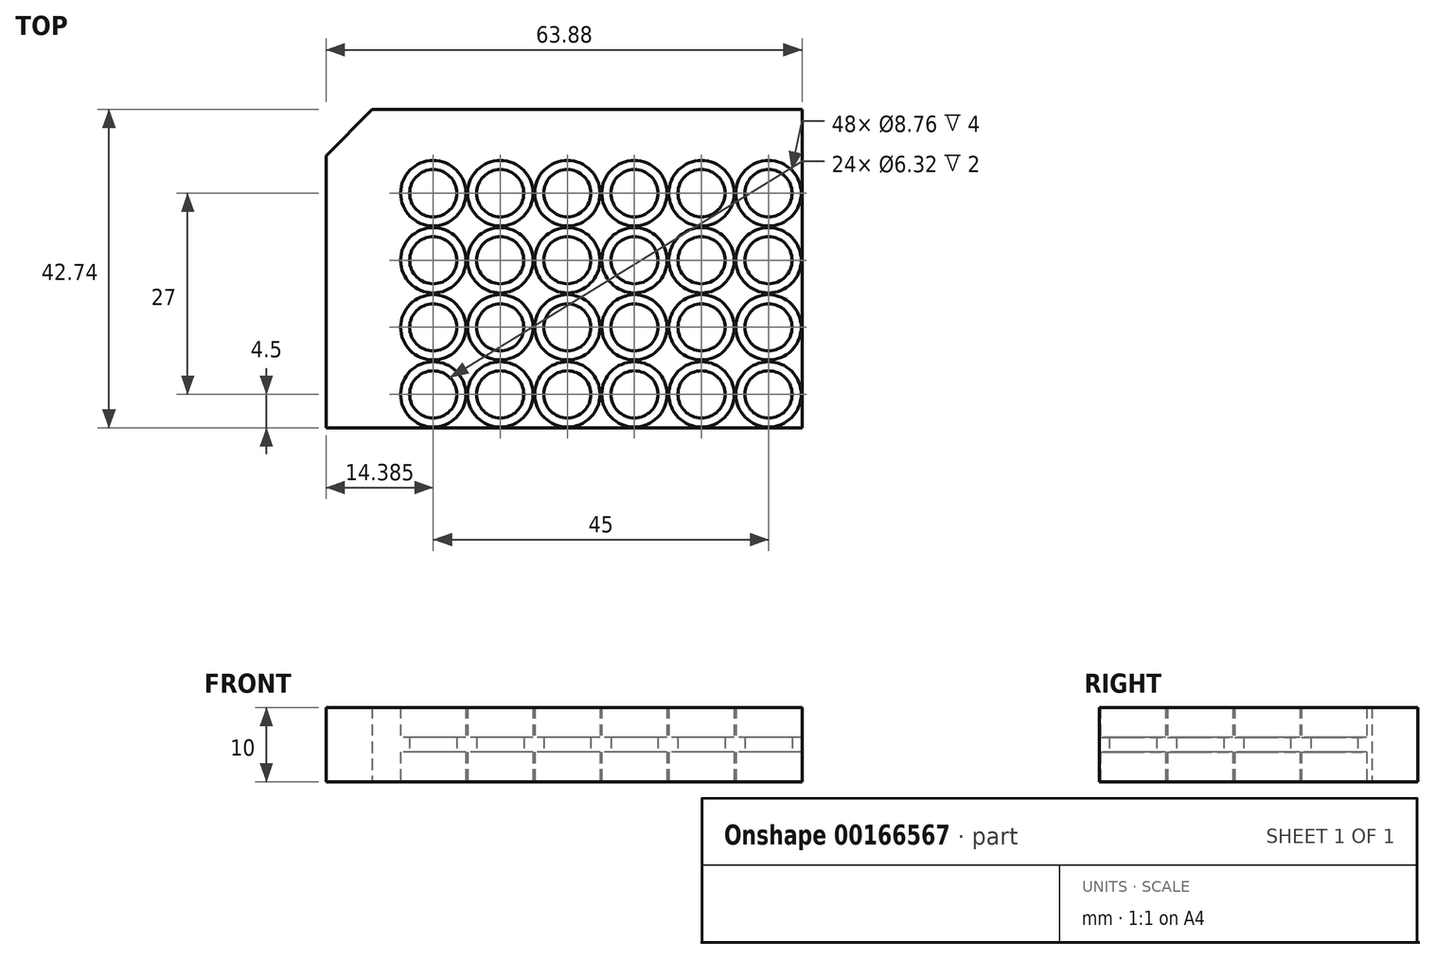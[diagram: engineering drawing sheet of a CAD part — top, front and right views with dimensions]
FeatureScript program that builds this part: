
annotation { "Feature Type Name" : "Feature", "Feature Type Description" : "" }
export const myFeature = defineFeature(function(context is Context, id is Id, definition is map)
    precondition{}
    {
        {
            var Q0;
            Q0=qCreatedBy(makeId("Top.planeOp"),FACE);
            var sketch = newSketch(context, id + "F0", { "sketchPlane" : qUnion([Q0])});
            skLineSegment(sketch, "E0", {"start": v(-63.88, 36.54) * mm, "end": v(-63.88, -36.54) * mm});
            skLineSegment(sketch, "E1", {"start": v(-63.88, -36.54) * mm, "end": v(-57.68, -42.74) * mm});
            skLineSegment(sketch, "E2", {"start": v(-57.68, -42.74) * mm, "end": v(63.88, -42.74) * mm});
            skLineSegment(sketch, "E3", {"start": v(63.88, -42.74) * mm, "end": v(63.88, 42.74) * mm});
            skLineSegment(sketch, "E4", {"start": v(63.88, 42.74) * mm, "end": v(-57.68, 42.74) * mm});
            skLineSegment(sketch, "E5", {"start": v(-57.68, 42.74) * mm, "end": v(-63.88, 36.54) * mm});
            skPoint(sketch, "E6", {"position": v(-63.87, 0) * mm});
            skLineSegment(sketch, "E7", {"start": v(-63.87, 0) * mm, "end": v(63.87, 0) * mm, "construction": true});
            skLineSegment(sketch, "E8", {"start": v(0, -42.74) * mm, "end": v(0, 42.74) * mm, "construction": true});
            skPoint(sketch, "E9", {"position": v(0, 0) * mm});
            skLineSegment(sketch, "E10", {"start": v(-63.88, 36.54) * mm, "end": v(-63.88, 42.74) * mm, "construction": true});
            skLineSegment(sketch, "E11", {"start": v(-63.88, 42.74) * mm, "end": v(-57.68, 42.74) * mm, "construction": true});
            skCircle(sketch, "E12", {"center": v(-49.5, 31.5) * mm, "radius": 3.16 * mm});
            skCircle(sketch, "E13.0.1.0", {"center": v(-49.5, 22.5) * mm, "radius": 3.16 * mm});
            skCircle(sketch, "E13.0.2.0", {"center": v(-49.5, 13.5) * mm, "radius": 3.16 * mm});
            skCircle(sketch, "E13.0.3.0", {"center": v(-49.5, 4.5) * mm, "radius": 3.16 * mm});
            skCircle(sketch, "E13.0.4.0", {"center": v(-49.5, -4.5) * mm, "radius": 3.16 * mm});
            skCircle(sketch, "E13.0.5.0", {"center": v(-49.5, -13.5) * mm, "radius": 3.16 * mm});
            skCircle(sketch, "E13.0.6.0", {"center": v(-49.5, -22.5) * mm, "radius": 3.16 * mm});
            skCircle(sketch, "E13.0.7.0", {"center": v(-49.5, -31.5) * mm, "radius": 3.16 * mm});
            skCircle(sketch, "E13.1.0.0", {"center": v(-40.5, 31.5) * mm, "radius": 3.16 * mm});
            skCircle(sketch, "E13.1.1.0", {"center": v(-40.5, 22.5) * mm, "radius": 3.16 * mm});
            skCircle(sketch, "E13.1.2.0", {"center": v(-40.5, 13.5) * mm, "radius": 3.16 * mm});
            skCircle(sketch, "E13.1.3.0", {"center": v(-40.5, 4.5) * mm, "radius": 3.16 * mm});
            skCircle(sketch, "E13.1.4.0", {"center": v(-40.5, -4.5) * mm, "radius": 3.16 * mm});
            skCircle(sketch, "E13.1.5.0", {"center": v(-40.5, -13.5) * mm, "radius": 3.16 * mm});
            skCircle(sketch, "E13.1.6.0", {"center": v(-40.5, -22.5) * mm, "radius": 3.16 * mm});
            skCircle(sketch, "E13.1.7.0", {"center": v(-40.5, -31.5) * mm, "radius": 3.16 * mm});
            skCircle(sketch, "E13.2.0.0", {"center": v(-31.5, 31.5) * mm, "radius": 3.16 * mm});
            skCircle(sketch, "E13.2.1.0", {"center": v(-31.5, 22.5) * mm, "radius": 3.16 * mm});
            skCircle(sketch, "E13.2.2.0", {"center": v(-31.5, 13.5) * mm, "radius": 3.16 * mm});
            skCircle(sketch, "E13.2.3.0", {"center": v(-31.5, 4.5) * mm, "radius": 3.16 * mm});
            skCircle(sketch, "E13.2.4.0", {"center": v(-31.5, -4.5) * mm, "radius": 3.16 * mm});
            skCircle(sketch, "E13.2.5.0", {"center": v(-31.5, -13.5) * mm, "radius": 3.16 * mm});
            skCircle(sketch, "E13.2.6.0", {"center": v(-31.5, -22.5) * mm, "radius": 3.16 * mm});
            skCircle(sketch, "E13.2.7.0", {"center": v(-31.5, -31.5) * mm, "radius": 3.16 * mm});
            skCircle(sketch, "E13.3.0.0", {"center": v(-22.5, 31.5) * mm, "radius": 3.16 * mm});
            skCircle(sketch, "E13.3.1.0", {"center": v(-22.5, 22.5) * mm, "radius": 3.16 * mm});
            skCircle(sketch, "E13.3.2.0", {"center": v(-22.5, 13.5) * mm, "radius": 3.16 * mm});
            skCircle(sketch, "E13.3.3.0", {"center": v(-22.5, 4.5) * mm, "radius": 3.16 * mm});
            skCircle(sketch, "E13.3.4.0", {"center": v(-22.5, -4.5) * mm, "radius": 3.16 * mm});
            skCircle(sketch, "E13.3.5.0", {"center": v(-22.5, -13.5) * mm, "radius": 3.16 * mm});
            skCircle(sketch, "E13.3.6.0", {"center": v(-22.5, -22.5) * mm, "radius": 3.16 * mm});
            skCircle(sketch, "E13.3.7.0", {"center": v(-22.5, -31.5) * mm, "radius": 3.16 * mm});
            skCircle(sketch, "E13.4.0.0", {"center": v(-13.5, 31.5) * mm, "radius": 3.16 * mm});
            skCircle(sketch, "E13.4.1.0", {"center": v(-13.5, 22.5) * mm, "radius": 3.16 * mm});
            skCircle(sketch, "E13.4.2.0", {"center": v(-13.5, 13.5) * mm, "radius": 3.16 * mm});
            skCircle(sketch, "E13.4.3.0", {"center": v(-13.5, 4.5) * mm, "radius": 3.16 * mm});
            skCircle(sketch, "E13.4.4.0", {"center": v(-13.5, -4.5) * mm, "radius": 3.16 * mm});
            skCircle(sketch, "E13.4.5.0", {"center": v(-13.5, -13.5) * mm, "radius": 3.16 * mm});
            skCircle(sketch, "E13.4.6.0", {"center": v(-13.5, -22.5) * mm, "radius": 3.16 * mm});
            skCircle(sketch, "E13.4.7.0", {"center": v(-13.5, -31.5) * mm, "radius": 3.16 * mm});
            skCircle(sketch, "E13.5.0.0", {"center": v(-4.5, 31.5) * mm, "radius": 3.16 * mm});
            skCircle(sketch, "E13.5.1.0", {"center": v(-4.5, 22.5) * mm, "radius": 3.16 * mm});
            skCircle(sketch, "E13.5.2.0", {"center": v(-4.5, 13.5) * mm, "radius": 3.16 * mm});
            skCircle(sketch, "E13.5.3.0", {"center": v(-4.5, 4.5) * mm, "radius": 3.16 * mm});
            skCircle(sketch, "E13.5.4.0", {"center": v(-4.5, -4.5) * mm, "radius": 3.16 * mm});
            skCircle(sketch, "E13.5.5.0", {"center": v(-4.5, -13.5) * mm, "radius": 3.16 * mm});
            skCircle(sketch, "E13.5.6.0", {"center": v(-4.5, -22.5) * mm, "radius": 3.16 * mm});
            skCircle(sketch, "E13.5.7.0", {"center": v(-4.5, -31.5) * mm, "radius": 3.16 * mm});
            skCircle(sketch, "E13.6.0.0", {"center": v(4.5, 31.5) * mm, "radius": 3.16 * mm});
            skCircle(sketch, "E13.6.1.0", {"center": v(4.5, 22.5) * mm, "radius": 3.16 * mm});
            skCircle(sketch, "E13.6.2.0", {"center": v(4.5, 13.5) * mm, "radius": 3.16 * mm});
            skCircle(sketch, "E13.6.3.0", {"center": v(4.5, 4.5) * mm, "radius": 3.16 * mm});
            skCircle(sketch, "E13.6.4.0", {"center": v(4.5, -4.5) * mm, "radius": 3.16 * mm});
            skCircle(sketch, "E13.6.5.0", {"center": v(4.5, -13.5) * mm, "radius": 3.16 * mm});
            skCircle(sketch, "E13.6.6.0", {"center": v(4.5, -22.5) * mm, "radius": 3.16 * mm});
            skCircle(sketch, "E13.6.7.0", {"center": v(4.5, -31.5) * mm, "radius": 3.16 * mm});
            skCircle(sketch, "E13.7.0.0", {"center": v(13.5, 31.5) * mm, "radius": 3.16 * mm});
            skCircle(sketch, "E13.7.1.0", {"center": v(13.5, 22.5) * mm, "radius": 3.16 * mm});
            skCircle(sketch, "E13.7.2.0", {"center": v(13.5, 13.5) * mm, "radius": 3.16 * mm});
            skCircle(sketch, "E13.7.3.0", {"center": v(13.5, 4.5) * mm, "radius": 3.16 * mm});
            skCircle(sketch, "E13.7.4.0", {"center": v(13.5, -4.5) * mm, "radius": 3.16 * mm});
            skCircle(sketch, "E13.7.5.0", {"center": v(13.5, -13.5) * mm, "radius": 3.16 * mm});
            skCircle(sketch, "E13.7.6.0", {"center": v(13.5, -22.5) * mm, "radius": 3.16 * mm});
            skCircle(sketch, "E13.7.7.0", {"center": v(13.5, -31.5) * mm, "radius": 3.16 * mm});
            skCircle(sketch, "E13.8.0.0", {"center": v(22.5, 31.5) * mm, "radius": 3.16 * mm});
            skCircle(sketch, "E13.8.1.0", {"center": v(22.5, 22.5) * mm, "radius": 3.16 * mm});
            skCircle(sketch, "E13.8.2.0", {"center": v(22.5, 13.5) * mm, "radius": 3.16 * mm});
            skCircle(sketch, "E13.8.3.0", {"center": v(22.5, 4.5) * mm, "radius": 3.16 * mm});
            skCircle(sketch, "E13.8.4.0", {"center": v(22.5, -4.5) * mm, "radius": 3.16 * mm});
            skCircle(sketch, "E13.8.5.0", {"center": v(22.5, -13.5) * mm, "radius": 3.16 * mm});
            skCircle(sketch, "E13.8.6.0", {"center": v(22.5, -22.5) * mm, "radius": 3.16 * mm});
            skCircle(sketch, "E13.8.7.0", {"center": v(22.5, -31.5) * mm, "radius": 3.16 * mm});
            skCircle(sketch, "E13.9.0.0", {"center": v(31.5, 31.5) * mm, "radius": 3.16 * mm});
            skCircle(sketch, "E13.9.1.0", {"center": v(31.5, 22.5) * mm, "radius": 3.16 * mm});
            skCircle(sketch, "E13.9.2.0", {"center": v(31.5, 13.5) * mm, "radius": 3.16 * mm});
            skCircle(sketch, "E13.9.3.0", {"center": v(31.5, 4.5) * mm, "radius": 3.16 * mm});
            skCircle(sketch, "E13.9.4.0", {"center": v(31.5, -4.5) * mm, "radius": 3.16 * mm});
            skCircle(sketch, "E13.9.5.0", {"center": v(31.5, -13.5) * mm, "radius": 3.16 * mm});
            skCircle(sketch, "E13.9.6.0", {"center": v(31.5, -22.5) * mm, "radius": 3.16 * mm});
            skCircle(sketch, "E13.9.7.0", {"center": v(31.5, -31.5) * mm, "radius": 3.16 * mm});
            skCircle(sketch, "E13.10.0.0", {"center": v(40.5, 31.5) * mm, "radius": 3.16 * mm});
            skCircle(sketch, "E13.10.1.0", {"center": v(40.5, 22.5) * mm, "radius": 3.16 * mm});
            skCircle(sketch, "E13.10.2.0", {"center": v(40.5, 13.5) * mm, "radius": 3.16 * mm});
            skCircle(sketch, "E13.10.3.0", {"center": v(40.5, 4.5) * mm, "radius": 3.16 * mm});
            skCircle(sketch, "E13.10.4.0", {"center": v(40.5, -4.5) * mm, "radius": 3.16 * mm});
            skCircle(sketch, "E13.10.5.0", {"center": v(40.5, -13.5) * mm, "radius": 3.16 * mm});
            skCircle(sketch, "E13.10.6.0", {"center": v(40.5, -22.5) * mm, "radius": 3.16 * mm});
            skCircle(sketch, "E13.10.7.0", {"center": v(40.5, -31.5) * mm, "radius": 3.16 * mm});
            skCircle(sketch, "E13.11.0.0", {"center": v(49.5, 31.5) * mm, "radius": 3.16 * mm});
            skCircle(sketch, "E13.11.1.0", {"center": v(49.5, 22.5) * mm, "radius": 3.16 * mm});
            skCircle(sketch, "E13.11.2.0", {"center": v(49.5, 13.5) * mm, "radius": 3.16 * mm});
            skCircle(sketch, "E13.11.3.0", {"center": v(49.5, 4.5) * mm, "radius": 3.16 * mm});
            skCircle(sketch, "E13.11.4.0", {"center": v(49.5, -4.5) * mm, "radius": 3.16 * mm});
            skCircle(sketch, "E13.11.5.0", {"center": v(49.5, -13.5) * mm, "radius": 3.16 * mm});
            skCircle(sketch, "E13.11.6.0", {"center": v(49.5, -22.5) * mm, "radius": 3.16 * mm});
            skCircle(sketch, "E13.11.7.0", {"center": v(49.5, -31.5) * mm, "radius": 3.16 * mm});
            skLineSegment(sketch, "E13.direction1", {"start": v(-49.5, 31.5) * mm, "end": v(-40.5, 31.5) * mm, "construction": true});
            skLineSegment(sketch, "E13.direction2", {"start": v(-49.5, 31.5) * mm, "end": v(-49.5, 22.5) * mm, "construction": true});
            skSolve(sketch);
        }
        {
            var Q0;
            Q0 = qSketchRegion(id + "F0", true);
            extrude(context, id + "F1", {"entities" : qUnion([Q0]), "depth" : 1 * mm, "hasSecondDirection" : true, "secondDirectionOppositeDirection" : true, "secondDirectionDepth" : 1 * mm});
        }
        {
            var Q0;
            Q0=qCreatedBy(makeId("Top.planeOp"),FACE);
            var sketch = newSketch(context, id + "F2", { "sketchPlane" : qUnion([Q0])});
            skCircle(sketch, "E14", {"center": v(-49.5, 31.5) * mm, "radius": 4.38 * mm});
            skCircle(sketch, "E15.0.1.0", {"center": v(-49.5, 22.5) * mm, "radius": 4.38 * mm});
            skCircle(sketch, "E15.0.2.0", {"center": v(-49.5, 13.5) * mm, "radius": 4.38 * mm});
            skCircle(sketch, "E15.0.3.0", {"center": v(-49.5, 4.5) * mm, "radius": 4.38 * mm});
            skCircle(sketch, "E15.0.4.0", {"center": v(-49.5, -4.5) * mm, "radius": 4.38 * mm});
            skCircle(sketch, "E15.0.5.0", {"center": v(-49.5, -13.5) * mm, "radius": 4.38 * mm});
            skCircle(sketch, "E15.0.6.0", {"center": v(-49.5, -22.5) * mm, "radius": 4.38 * mm});
            skCircle(sketch, "E15.0.7.0", {"center": v(-49.5, -31.5) * mm, "radius": 4.38 * mm});
            skCircle(sketch, "E15.1.0.0", {"center": v(-40.5, 31.5) * mm, "radius": 4.38 * mm});
            skCircle(sketch, "E15.1.1.0", {"center": v(-40.5, 22.5) * mm, "radius": 4.38 * mm});
            skCircle(sketch, "E15.1.2.0", {"center": v(-40.5, 13.5) * mm, "radius": 4.38 * mm});
            skCircle(sketch, "E15.1.3.0", {"center": v(-40.5, 4.5) * mm, "radius": 4.38 * mm});
            skCircle(sketch, "E15.1.4.0", {"center": v(-40.5, -4.5) * mm, "radius": 4.38 * mm});
            skCircle(sketch, "E15.1.5.0", {"center": v(-40.5, -13.5) * mm, "radius": 4.38 * mm});
            skCircle(sketch, "E15.1.6.0", {"center": v(-40.5, -22.5) * mm, "radius": 4.38 * mm});
            skCircle(sketch, "E15.1.7.0", {"center": v(-40.5, -31.5) * mm, "radius": 4.38 * mm});
            skCircle(sketch, "E15.2.0.0", {"center": v(-31.5, 31.5) * mm, "radius": 4.38 * mm});
            skCircle(sketch, "E15.2.1.0", {"center": v(-31.5, 22.5) * mm, "radius": 4.38 * mm});
            skCircle(sketch, "E15.2.2.0", {"center": v(-31.5, 13.5) * mm, "radius": 4.38 * mm});
            skCircle(sketch, "E15.2.3.0", {"center": v(-31.5, 4.5) * mm, "radius": 4.38 * mm});
            skCircle(sketch, "E15.2.4.0", {"center": v(-31.5, -4.5) * mm, "radius": 4.38 * mm});
            skCircle(sketch, "E15.2.5.0", {"center": v(-31.5, -13.5) * mm, "radius": 4.38 * mm});
            skCircle(sketch, "E15.2.6.0", {"center": v(-31.5, -22.5) * mm, "radius": 4.38 * mm});
            skCircle(sketch, "E15.2.7.0", {"center": v(-31.5, -31.5) * mm, "radius": 4.38 * mm});
            skCircle(sketch, "E15.3.0.0", {"center": v(-22.5, 31.5) * mm, "radius": 4.38 * mm});
            skCircle(sketch, "E15.3.1.0", {"center": v(-22.5, 22.5) * mm, "radius": 4.38 * mm});
            skCircle(sketch, "E15.3.2.0", {"center": v(-22.5, 13.5) * mm, "radius": 4.38 * mm});
            skCircle(sketch, "E15.3.3.0", {"center": v(-22.5, 4.5) * mm, "radius": 4.38 * mm});
            skCircle(sketch, "E15.3.4.0", {"center": v(-22.5, -4.5) * mm, "radius": 4.38 * mm});
            skCircle(sketch, "E15.3.5.0", {"center": v(-22.5, -13.5) * mm, "radius": 4.38 * mm});
            skCircle(sketch, "E15.3.6.0", {"center": v(-22.5, -22.5) * mm, "radius": 4.38 * mm});
            skCircle(sketch, "E15.3.7.0", {"center": v(-22.5, -31.5) * mm, "radius": 4.38 * mm});
            skCircle(sketch, "E15.4.0.0", {"center": v(-13.5, 31.5) * mm, "radius": 4.38 * mm});
            skCircle(sketch, "E15.4.1.0", {"center": v(-13.5, 22.5) * mm, "radius": 4.38 * mm});
            skCircle(sketch, "E15.4.2.0", {"center": v(-13.5, 13.5) * mm, "radius": 4.38 * mm});
            skCircle(sketch, "E15.4.3.0", {"center": v(-13.5, 4.5) * mm, "radius": 4.38 * mm});
            skCircle(sketch, "E15.4.4.0", {"center": v(-13.5, -4.5) * mm, "radius": 4.38 * mm});
            skCircle(sketch, "E15.4.5.0", {"center": v(-13.5, -13.5) * mm, "radius": 4.38 * mm});
            skCircle(sketch, "E15.4.6.0", {"center": v(-13.5, -22.5) * mm, "radius": 4.38 * mm});
            skCircle(sketch, "E15.4.7.0", {"center": v(-13.5, -31.5) * mm, "radius": 4.38 * mm});
            skCircle(sketch, "E15.5.0.0", {"center": v(-4.5, 31.5) * mm, "radius": 4.38 * mm});
            skCircle(sketch, "E15.5.1.0", {"center": v(-4.5, 22.5) * mm, "radius": 4.38 * mm});
            skCircle(sketch, "E15.5.2.0", {"center": v(-4.5, 13.5) * mm, "radius": 4.38 * mm});
            skCircle(sketch, "E15.5.3.0", {"center": v(-4.5, 4.5) * mm, "radius": 4.38 * mm});
            skCircle(sketch, "E15.5.4.0", {"center": v(-4.5, -4.5) * mm, "radius": 4.38 * mm});
            skCircle(sketch, "E15.5.5.0", {"center": v(-4.5, -13.5) * mm, "radius": 4.38 * mm});
            skCircle(sketch, "E15.5.6.0", {"center": v(-4.5, -22.5) * mm, "radius": 4.38 * mm});
            skCircle(sketch, "E15.5.7.0", {"center": v(-4.5, -31.5) * mm, "radius": 4.38 * mm});
            skCircle(sketch, "E15.6.0.0", {"center": v(4.5, 31.5) * mm, "radius": 4.38 * mm});
            skCircle(sketch, "E15.6.1.0", {"center": v(4.5, 22.5) * mm, "radius": 4.38 * mm});
            skCircle(sketch, "E15.6.2.0", {"center": v(4.5, 13.5) * mm, "radius": 4.38 * mm});
            skCircle(sketch, "E15.6.3.0", {"center": v(4.5, 4.5) * mm, "radius": 4.38 * mm});
            skCircle(sketch, "E15.6.4.0", {"center": v(4.5, -4.5) * mm, "radius": 4.38 * mm});
            skCircle(sketch, "E15.6.5.0", {"center": v(4.5, -13.5) * mm, "radius": 4.38 * mm});
            skCircle(sketch, "E15.6.6.0", {"center": v(4.5, -22.5) * mm, "radius": 4.38 * mm});
            skCircle(sketch, "E15.6.7.0", {"center": v(4.5, -31.5) * mm, "radius": 4.38 * mm});
            skCircle(sketch, "E15.7.0.0", {"center": v(13.5, 31.5) * mm, "radius": 4.38 * mm});
            skCircle(sketch, "E15.7.1.0", {"center": v(13.5, 22.5) * mm, "radius": 4.38 * mm});
            skCircle(sketch, "E15.7.2.0", {"center": v(13.5, 13.5) * mm, "radius": 4.38 * mm});
            skCircle(sketch, "E15.7.3.0", {"center": v(13.5, 4.5) * mm, "radius": 4.38 * mm});
            skCircle(sketch, "E15.7.4.0", {"center": v(13.5, -4.5) * mm, "radius": 4.38 * mm});
            skCircle(sketch, "E15.7.5.0", {"center": v(13.5, -13.5) * mm, "radius": 4.38 * mm});
            skCircle(sketch, "E15.7.6.0", {"center": v(13.5, -22.5) * mm, "radius": 4.38 * mm});
            skCircle(sketch, "E15.7.7.0", {"center": v(13.5, -31.5) * mm, "radius": 4.38 * mm});
            skCircle(sketch, "E15.8.0.0", {"center": v(22.5, 31.5) * mm, "radius": 4.38 * mm});
            skCircle(sketch, "E15.8.1.0", {"center": v(22.5, 22.5) * mm, "radius": 4.38 * mm});
            skCircle(sketch, "E15.8.2.0", {"center": v(22.5, 13.5) * mm, "radius": 4.38 * mm});
            skCircle(sketch, "E15.8.3.0", {"center": v(22.5, 4.5) * mm, "radius": 4.38 * mm});
            skCircle(sketch, "E15.8.4.0", {"center": v(22.5, -4.5) * mm, "radius": 4.38 * mm});
            skCircle(sketch, "E15.8.5.0", {"center": v(22.5, -13.5) * mm, "radius": 4.38 * mm});
            skCircle(sketch, "E15.8.6.0", {"center": v(22.5, -22.5) * mm, "radius": 4.38 * mm});
            skCircle(sketch, "E15.8.7.0", {"center": v(22.5, -31.5) * mm, "radius": 4.38 * mm});
            skCircle(sketch, "E15.9.0.0", {"center": v(31.5, 31.5) * mm, "radius": 4.38 * mm});
            skCircle(sketch, "E15.9.1.0", {"center": v(31.5, 22.5) * mm, "radius": 4.38 * mm});
            skCircle(sketch, "E15.9.2.0", {"center": v(31.5, 13.5) * mm, "radius": 4.38 * mm});
            skCircle(sketch, "E15.9.3.0", {"center": v(31.5, 4.5) * mm, "radius": 4.38 * mm});
            skCircle(sketch, "E15.9.4.0", {"center": v(31.5, -4.5) * mm, "radius": 4.38 * mm});
            skCircle(sketch, "E15.9.5.0", {"center": v(31.5, -13.5) * mm, "radius": 4.38 * mm});
            skCircle(sketch, "E15.9.6.0", {"center": v(31.5, -22.5) * mm, "radius": 4.38 * mm});
            skCircle(sketch, "E15.9.7.0", {"center": v(31.5, -31.5) * mm, "radius": 4.38 * mm});
            skCircle(sketch, "E15.10.0.0", {"center": v(40.5, 31.5) * mm, "radius": 4.38 * mm});
            skCircle(sketch, "E15.10.1.0", {"center": v(40.5, 22.5) * mm, "radius": 4.38 * mm});
            skCircle(sketch, "E15.10.2.0", {"center": v(40.5, 13.5) * mm, "radius": 4.38 * mm});
            skCircle(sketch, "E15.10.3.0", {"center": v(40.5, 4.5) * mm, "radius": 4.38 * mm});
            skCircle(sketch, "E15.10.4.0", {"center": v(40.5, -4.5) * mm, "radius": 4.38 * mm});
            skCircle(sketch, "E15.10.5.0", {"center": v(40.5, -13.5) * mm, "radius": 4.38 * mm});
            skCircle(sketch, "E15.10.6.0", {"center": v(40.5, -22.5) * mm, "radius": 4.38 * mm});
            skCircle(sketch, "E15.10.7.0", {"center": v(40.5, -31.5) * mm, "radius": 4.38 * mm});
            skCircle(sketch, "E15.11.0.0", {"center": v(49.5, 31.5) * mm, "radius": 4.38 * mm});
            skCircle(sketch, "E15.11.1.0", {"center": v(49.5, 22.5) * mm, "radius": 4.38 * mm});
            skCircle(sketch, "E15.11.2.0", {"center": v(49.5, 13.5) * mm, "radius": 4.38 * mm});
            skCircle(sketch, "E15.11.3.0", {"center": v(49.5, 4.5) * mm, "radius": 4.38 * mm});
            skCircle(sketch, "E15.11.4.0", {"center": v(49.5, -4.5) * mm, "radius": 4.38 * mm});
            skCircle(sketch, "E15.11.5.0", {"center": v(49.5, -13.5) * mm, "radius": 4.38 * mm});
            skCircle(sketch, "E15.11.6.0", {"center": v(49.5, -22.5) * mm, "radius": 4.38 * mm});
            skCircle(sketch, "E15.11.7.0", {"center": v(49.5, -31.5) * mm, "radius": 4.38 * mm});
            skLineSegment(sketch, "E15.direction1", {"start": v(-49.5, 31.5) * mm, "end": v(-40.5, 31.5) * mm, "construction": true});
            skLineSegment(sketch, "E15.direction2", {"start": v(-49.5, 31.5) * mm, "end": v(-49.5, 22.5) * mm, "construction": true});
            skLineSegment(sketch, "E16", {"start": v(63.88, 42.74) * mm, "end": v(63.88, -42.74) * mm});
            skLineSegment(sketch, "E17", {"start": v(63.88, -42.74) * mm, "end": v(-57.68, -42.74) * mm});
            skLineSegment(sketch, "E18", {"start": v(-57.68, -42.74) * mm, "end": v(-63.87, -36.54) * mm});
            skLineSegment(sketch, "E19", {"start": v(-63.88, -36.54) * mm, "end": v(-63.88, 36.54) * mm});
            skLineSegment(sketch, "E20", {"start": v(-63.88, 36.54) * mm, "end": v(-57.68, 42.74) * mm});
            skLineSegment(sketch, "E21", {"start": v(-57.68, 42.74) * mm, "end": v(63.88, 42.74) * mm});
            skSolve(sketch);
        }
        {
            var Q0;
            Q0 = qSketchRegion(id + "F2", true);
            extrude(context, id + "F3", {"entities" : qUnion([Q0]), "operationType" : NewBodyOperationType.ADD, "depth" : 5 * mm, "hasSecondDirection" : true, "secondDirectionOppositeDirection" : true, "secondDirectionDepth" : 5 * mm});
        }
        {
            var Q0;
            Q0=qCreatedBy(makeId("Top.planeOp"),FACE);
            var sketch = newSketch(context, id + "F4", { "sketchPlane" : qUnion([Q0])});
            skLineSegment(sketch, "E22.bottom", {"start": v(0, 0) * mm, "end": v(-70.7, 0) * mm});
            skLineSegment(sketch, "E22.top", {"start": v(0, -43.57) * mm, "end": v(-70.7, -43.57) * mm});
            skLineSegment(sketch, "E22.left", {"start": v(0, 0) * mm, "end": v(0, -43.57) * mm});
            skLineSegment(sketch, "E22.right", {"start": v(-70.7, 0) * mm, "end": v(-70.7, -43.57) * mm});
            skLineSegment(sketch, "E23.bottom", {"start": v(0, -43.57) * mm, "end": v(65.9, -43.57) * mm});
            skLineSegment(sketch, "E23.top", {"start": v(0, 44.06) * mm, "end": v(65.9, 44.06) * mm});
            skLineSegment(sketch, "E23.left", {"start": v(0, -43.57) * mm, "end": v(0, 44.06) * mm});
            skLineSegment(sketch, "E23.right", {"start": v(65.9, -43.57) * mm, "end": v(65.9, 44.06) * mm});
            skSolve(sketch);
        }
        {
            var Q0;
            Q0 = qSketchRegion(id + "F4", true);
            extrude(context, id + "F5", {"entities" : qUnion([Q0]), "operationType" : NewBodyOperationType.REMOVE, "oppositeDirection" : true, "depth" : 25.4 * mm, "hasSecondDirection" : true, "secondDirectionOppositeDirection" : false, "secondDirectionDepth" : 25.4 * mm});
        }
    });
